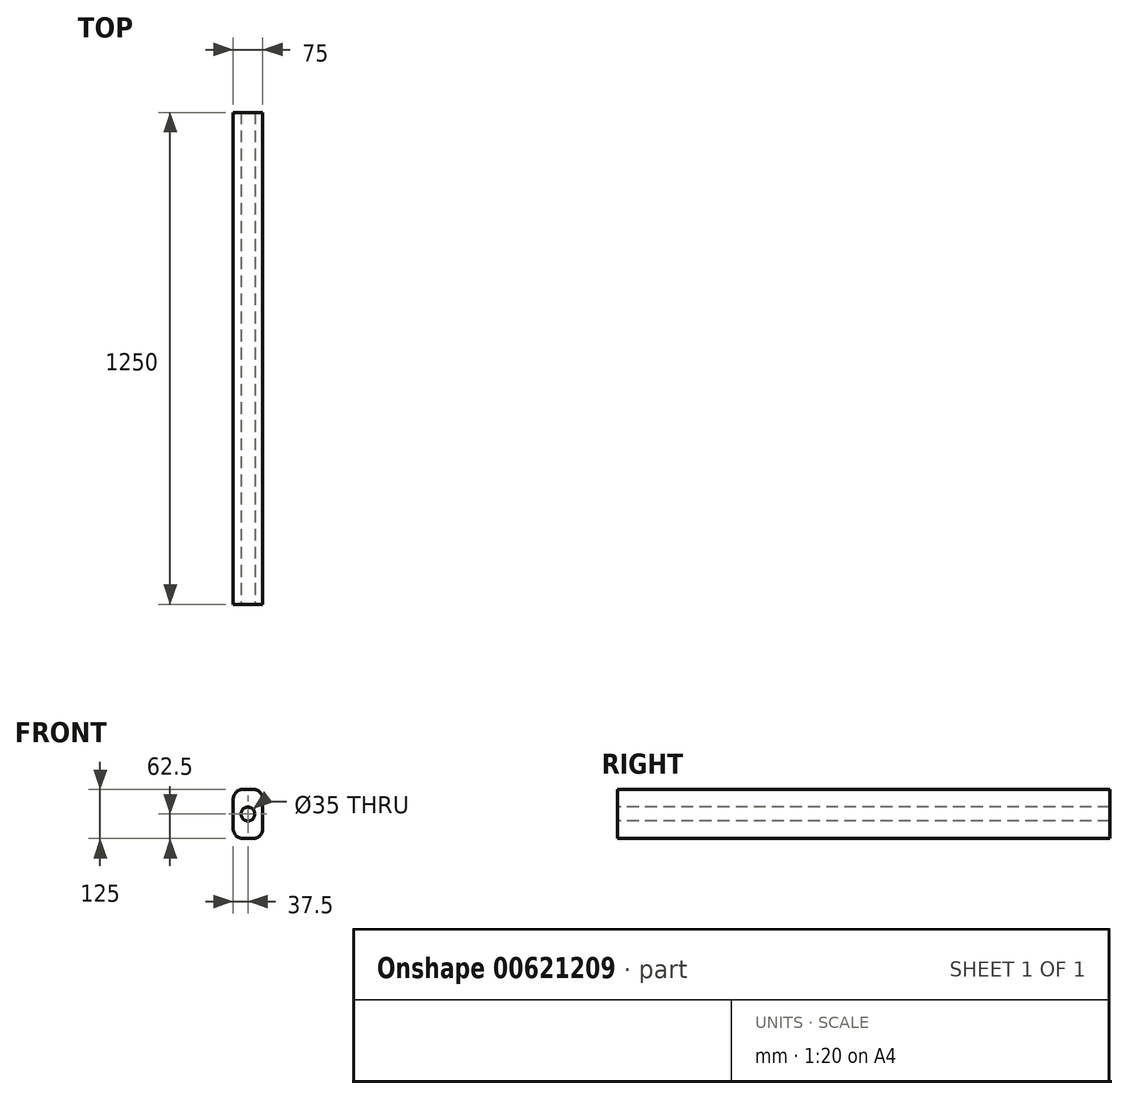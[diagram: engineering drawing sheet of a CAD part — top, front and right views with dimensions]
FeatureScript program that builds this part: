
annotation { "Feature Type Name" : "Feature", "Feature Type Description" : "" }
export const myFeature = defineFeature(function(context is Context, id is Id, definition is map)
    precondition{}
    {
        {
            var Q0;
            Q0=qCreatedBy(makeId("Front.planeOp"),FACE);
            var sketch = newSketch(context, id + "F0", { "sketchPlane" : qUnion([Q0])});
            skLineSegment(sketch, "E0.bottom", {"start": v(-37.5, 62.5) * mm, "end": v(37.5, 62.5) * mm});
            skLineSegment(sketch, "E0.top", {"start": v(-37.5, -62.5) * mm, "end": v(37.5, -62.5) * mm});
            skLineSegment(sketch, "E0.left", {"start": v(-37.5, 62.5) * mm, "end": v(-37.5, -62.5) * mm});
            skLineSegment(sketch, "E0.right", {"start": v(37.5, 62.5) * mm, "end": v(37.5, -62.5) * mm});
            skSolve(sketch);
        }
        {
            var Q0;
            Q0=makeQuery(id+"F0.imprint","IMPRINT",FACE,{"disambiguationData":[TD([[makeQuery(id+"F0.imprint","IMPRINT",EDGE,{"derivedFrom":sQuery(id+"F0.wireOp",EDGE,"E0.bottom")}),-1.0]])]});
            extrude(context, id + "F1", {"entities" : qUnion([Q0]), "endBound" : BoundingType.SYMMETRIC, "depth" : 1250 * mm, "offsetDistance" : 25 * mm});
        }
        {
            var Q0;
            Q0=makeQuery(id+"F1.opExtrude","CAP_FACE",FACE,{"disambiguationData":[OSD([sQuery(id+"F0.wireOp",EDGE,"E0.bottom"),sQuery(id+"F0.wireOp",EDGE,"E0.top"),sQuery(id+"F0.wireOp",EDGE,"E0.left"),sQuery(id+"F0.wireOp",EDGE,"E0.right")])],"isStart":false});
            var sketch = newSketch(context, id + "F2", { "sketchPlane" : qUnion([Q0])});
            skCircle(sketch, "E1", {"center": v(0, 0) * mm, "radius": 17.5 * mm});
            skSolve(sketch);
        }
        {
            var Q0;
            Q0=makeQuery(id+"F2.imprint","IMPRINT",FACE,{"disambiguationData":[TD([[makeQuery(id+"F2.imprint","IMPRINT",EDGE,{"derivedFrom":sQuery(id+"F2.wireOp",EDGE,"E1")}),1.0]])]});
            extrude(context, id + "F3", {"entities" : qUnion([Q0]), "operationType" : NewBodyOperationType.REMOVE, "oppositeDirection" : true, "depth" : 1250 * mm, "offsetDistance" : 25 * mm});
        }
        {
            var Q0;
            Q0=makeQuery(id+"F1.opExtrude","SWEPT_EDGE",EDGE,{"disambiguationData":[OSD([sQuery(id+"F0.wireOp",EDGE,"E0.bottom"),sQuery(id+"F0.wireOp",EDGE,"E0.right")])]});
            var Q1;
            Q1=makeQuery(id+"F1.opExtrude","SWEPT_EDGE",EDGE,{"disambiguationData":[OSD([sQuery(id+"F0.wireOp",EDGE,"E0.bottom"),sQuery(id+"F0.wireOp",EDGE,"E0.left")])]});
            var Q2;
            Q2=makeQuery(id+"F1.opExtrude","SWEPT_EDGE",EDGE,{"disambiguationData":[OSD([sQuery(id+"F0.wireOp",EDGE,"E0.top"),sQuery(id+"F0.wireOp",EDGE,"E0.left")])]});
            var Q3;
            Q3=makeQuery(id+"F1.opExtrude","SWEPT_EDGE",EDGE,{"disambiguationData":[OSD([sQuery(id+"F0.wireOp",EDGE,"E0.top"),sQuery(id+"F0.wireOp",EDGE,"E0.right")])]});
            fillet(context, id + "F4", {"entities" : qUnion([Q0, Q1, Q2, Q3]), "radius" : 25 * mm, "tangentPropagation" : true, "allowEdgeOverflow" : false});
        }
    });
